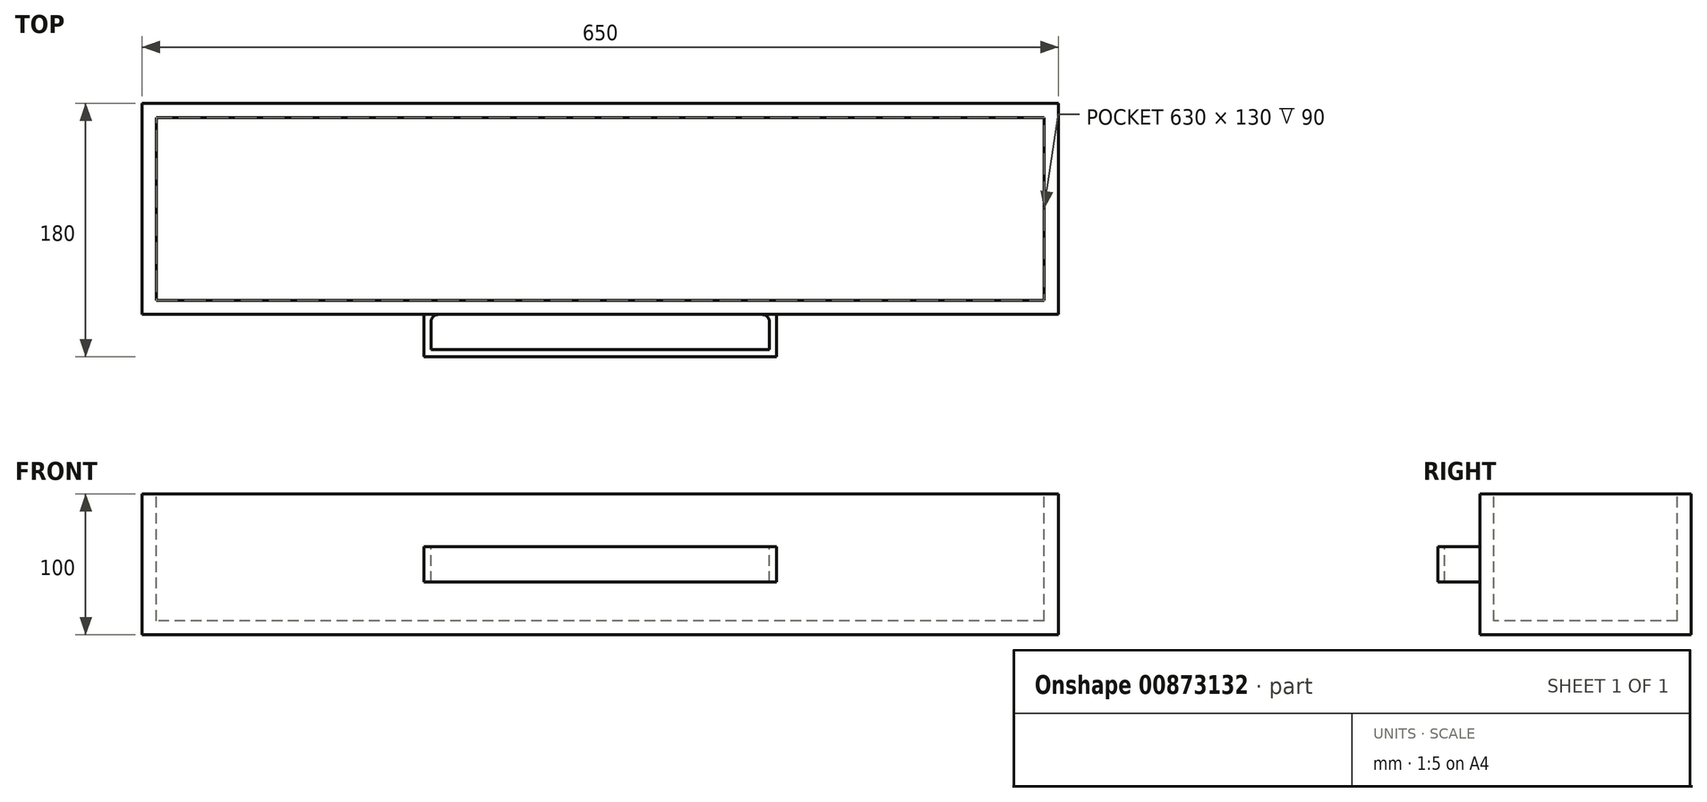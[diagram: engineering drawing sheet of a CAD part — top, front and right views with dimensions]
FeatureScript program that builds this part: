
annotation { "Feature Type Name" : "Feature", "Feature Type Description" : "" }
export const myFeature = defineFeature(function(context is Context, id is Id, definition is map)
    precondition{}
    {
        {
            var Q0;
            Q0=qCreatedBy(makeId("Front.planeOp"),FACE);
            var sketch = newSketch(context, id + "F0", { "sketchPlane" : qUnion([Q0])});
            skLineSegment(sketch, "E0.bottom", {"start": v(325, -50) * mm, "end": v(-325, -50) * mm});
            skLineSegment(sketch, "E0.top", {"start": v(325, 50) * mm, "end": v(-325, 50) * mm});
            skLineSegment(sketch, "E0.left", {"start": v(325, -50) * mm, "end": v(325, 50) * mm});
            skLineSegment(sketch, "E0.right", {"start": v(-325, -50) * mm, "end": v(-325, 50) * mm});
            skPoint(sketch, "E0.middle", {"position": v(0, 0) * mm});
            skSolve(sketch);
        }
        {
            var Q0;
            Q0=makeQuery(id+"F0.imprint","IMPRINT",FACE,{"disambiguationData":[TD([[makeQuery(id+"F0.imprint","IMPRINT",EDGE,{"derivedFrom":sQuery(id+"F0.wireOp",EDGE,"E0.bottom")}),-1.0]])]});
            extrude(context, id + "F1", {"entities" : qUnion([Q0]), "depth" : 150 * mm, "offsetDistance" : 25 * mm});
        }
        {
            var Q0;
            Q0=makeQuery(id+"F1.opExtrude","CAP_FACE",FACE,{"disambiguationData":[OSD([sQuery(id+"F0.wireOp",EDGE,"E0.bottom"),sQuery(id+"F0.wireOp",EDGE,"E0.top"),sQuery(id+"F0.wireOp",EDGE,"E0.left"),sQuery(id+"F0.wireOp",EDGE,"E0.right")])],"isStart":false});
            var sketch = newSketch(context, id + "F2", { "sketchPlane" : qUnion([Q0])});
            skLineSegment(sketch, "E1.bottom", {"start": v(125, -12.5) * mm, "end": v(-125, -12.5) * mm});
            skLineSegment(sketch, "E1.top", {"start": v(125, 12.5) * mm, "end": v(-125, 12.5) * mm});
            skLineSegment(sketch, "E1.left", {"start": v(125, -12.5) * mm, "end": v(125, 12.5) * mm});
            skLineSegment(sketch, "E1.right", {"start": v(-125, -12.5) * mm, "end": v(-125, 12.5) * mm});
            skPoint(sketch, "E1.middle", {"position": v(0, 0) * mm});
            skSolve(sketch);
        }
        {
            var Q0;
            Q0 = qSketchRegion(id + "F2", true);
            extrude(context, id + "F3", {"entities" : qUnion([Q0]), "operationType" : NewBodyOperationType.ADD, "depth" : 30 * mm, "offsetDistance" : 25 * mm});
        }
        {
            var Q0;
            Q0=makeQuery(id+"F3.opExtrude","SWEPT_FACE",FACE,{"disambiguationData":[OSD([sQuery(id+"F2.wireOp",EDGE,"E1.top")])]});
            var sketch = newSketch(context, id + "F4", { "sketchPlane" : qUnion([Q0])});
            skLineSegment(sketch, "E2.bottom", {"start": v(120, -175) * mm, "end": v(-120, -175) * mm});
            skLineSegment(sketch, "E2.left", {"start": v(120, -175) * mm, "end": v(120, -155) * mm});
            skLineSegment(sketch, "E2.right", {"start": v(-120, -175) * mm, "end": v(-120, -155) * mm});
            skPoint(sketch, "E2.middle", {"position": v(0, -165) * mm});
            skPoint(sketch, "E2.middle.positionSnap0", {"position": v(125, -165) * mm});
            skPoint(sketch, "E2.middle.positionSnap1", {"position": v(0, -180) * mm});
            skPoint(sketch, "E2.centerSnap0", {"position": v(125, -165) * mm});
            skPoint(sketch, "E2.centerSnap1", {"position": v(0, -180) * mm});
            skLineSegment(sketch, "E3", {"start": v(-120, -155) * mm, "end": v(-120, -150) * mm});
            skLineSegment(sketch, "E4", {"start": v(-120, -150) * mm, "end": v(120, -150) * mm});
            skLineSegment(sketch, "E5", {"start": v(120, -150) * mm, "end": v(120, -155) * mm});
            skSolve(sketch);
        }
        {
            var Q0;
            Q0 = qSketchRegion(id + "F4", true);
            extrude(context, id + "F5", {"entities" : qUnion([Q0]), "operationType" : NewBodyOperationType.REMOVE, "oppositeDirection" : true, "depth" : 25 * mm, "offsetDistance" : 25 * mm});
        }
        {
            var Q0;
            Q0=makeQuery(id+"F3.opExtrude","CAP_EDGE",EDGE,{"disambiguationData":[OSD([sQuery(id+"F2.wireOp",EDGE,"E1.left")])],"isStart":true});
            var Q1;
            Q1=makeQuery(id+"F3.opExtrude","CAP_EDGE",EDGE,{"disambiguationData":[OSD([sQuery(id+"F2.wireOp",EDGE,"E1.right")])],"isStart":true});
            var Q2;
            {var subQ0=sQuery(id+"F2.wireOp",EDGE,"E1.top");Q2=makeQuery(id+"F5.boolean.opBoolean","SPLIT",EDGE,{"disambiguationData":[TD([makeQuery(id+"F3.opExtrude","SWEPT_FACE",FACE,{"disambiguationData":[OSD([sQuery(id+"F2.wireOp",EDGE,"E1.right")])]})])],"derivedFrom":makeQuery(id+"F3.opExtrude","CAP_EDGE",EDGE,{"disambiguationData":[OSD([subQ0])],"isStart":true})});}
            var Q3;
            {var subQ0=sQuery(id+"F2.wireOp",EDGE,"E1.bottom");Q3=makeQuery(id+"F5.boolean.opBoolean","SPLIT",EDGE,{"disambiguationData":[TD([makeQuery(id+"F3.opExtrude","SWEPT_FACE",FACE,{"disambiguationData":[OSD([sQuery(id+"F2.wireOp",EDGE,"E1.right")])]})])],"derivedFrom":makeQuery(id+"F3.opExtrude","CAP_EDGE",EDGE,{"disambiguationData":[OSD([subQ0])],"isStart":true})});}
            var Q4;
            Q4=makeQuery(id+"F5.boolean.opBoolean","COPY",EDGE,{"derivedFrom":makeQuery(id+"F5.opExtrude","SWEPT_EDGE",EDGE,{"disambiguationData":[OSD([sQuery(id+"F2.wireOp",EDGE,"E1.top"),sQuery(id+"F4.wireOp",EDGE,"E3"),sQuery(id+"F4.wireOp",EDGE,"E4")])]})});
            var Q5;
            Q5=makeQuery(id+"F5.boolean.opBoolean","COPY",EDGE,{"derivedFrom":makeQuery(id+"F5.opExtrude","SWEPT_EDGE",EDGE,{"disambiguationData":[OSD([sQuery(id+"F2.wireOp",EDGE,"E1.top"),sQuery(id+"F4.wireOp",EDGE,"E4"),sQuery(id+"F4.wireOp",EDGE,"E5")])]})});
            var Q6;
            {var subQ0=sQuery(id+"F2.wireOp",EDGE,"E1.bottom");Q6=makeQuery(id+"F5.boolean.opBoolean","SPLIT",EDGE,{"disambiguationData":[TD([makeQuery(id+"F3.opExtrude","SWEPT_FACE",FACE,{"disambiguationData":[OSD([sQuery(id+"F2.wireOp",EDGE,"E1.left")])]})])],"derivedFrom":makeQuery(id+"F3.opExtrude","CAP_EDGE",EDGE,{"disambiguationData":[OSD([subQ0])],"isStart":true})});}
            var Q7;
            {var subQ0=sQuery(id+"F2.wireOp",EDGE,"E1.top");Q7=makeQuery(id+"F5.boolean.opBoolean","SPLIT",EDGE,{"disambiguationData":[TD([makeQuery(id+"F3.opExtrude","SWEPT_FACE",FACE,{"disambiguationData":[OSD([sQuery(id+"F2.wireOp",EDGE,"E1.left")])]})])],"derivedFrom":makeQuery(id+"F3.opExtrude","CAP_EDGE",EDGE,{"disambiguationData":[OSD([subQ0])],"isStart":true})});}
            fillet(context, id + "F6", {"entities" : qUnion([Q0, Q1, Q2, Q3, Q4, Q5, Q6, Q7]), "radius" : 5 * mm, "tangentPropagation" : true, "allowEdgeOverflow" : false});
        }
        {
            var Q0;
            Q0=makeQuery(id+"F1.opExtrude","SWEPT_FACE",FACE,{"disambiguationData":[OSD([sQuery(id+"F0.wireOp",EDGE,"E0.top")])]});
            var sketch = newSketch(context, id + "F7", { "sketchPlane" : qUnion([Q0])});
            skLineSegment(sketch, "E6.bottom", {"start": v(315, -10) * mm, "end": v(-315, -10) * mm});
            skLineSegment(sketch, "E6.top", {"start": v(315, -140) * mm, "end": v(-315, -140) * mm});
            skLineSegment(sketch, "E6.left", {"start": v(315, -10) * mm, "end": v(315, -140) * mm});
            skLineSegment(sketch, "E6.right", {"start": v(-315, -10) * mm, "end": v(-315, -140) * mm});
            skPoint(sketch, "E6.middle", {"position": v(0, -75) * mm});
            skPoint(sketch, "E6.middle.positionSnap0", {"position": v(-325, -75) * mm});
            skPoint(sketch, "E6.centerSnap0", {"position": v(-325, -75) * mm});
            skSolve(sketch);
        }
        {
            var Q0;
            Q0=makeQuery(id+"F7.imprint","IMPRINT",FACE,{"disambiguationData":[TD([[makeQuery(id+"F7.imprint","IMPRINT",EDGE,{"derivedFrom":sQuery(id+"F7.wireOp",EDGE,"E6.bottom")}),1.0]])]});
            extrude(context, id + "F8", {"entities" : qUnion([Q0]), "operationType" : NewBodyOperationType.REMOVE, "oppositeDirection" : true, "depth" : 90 * mm, "offsetDistance" : 25 * mm});
        }
    });
